# Revit family: IS_Concept_Multiproduct_BIM_GB_E0319;E0320
name_source: partatom
category: Casework
revit_build: Autodesk Revit 2015 (Build: 20140606_1530(x64)
units: mm (PartAtom-declared; Revit-internal decimal feet)

## types (4) — shared parameters
Accessories = www.idealspec.co.uk
AreaUnits = millimeters
Assembly Code = C1030200
AssetType = Fixed
Brand = Ideal Standard
CodePerformance = FSC, EN 14749:2005
ConnectionType = Mechanical
Default Elevation = 2000 mm
Depth = 170 mm
DurationUnit = year
ExpectedLife = 30
Height = 700 mm
IfcExportAs = IfcFurnitureType
IfcExportType = Bathroom cabinets
InstallationInstructions = www.idealspec.co.uk/resources.html
LinearUnits = millimeters
ManufacturerURL = www.idealspec.co.uk
Material = Varies, see product information
MetalMtl = ISI_IdealStandard_Furniture_Metal_Chrome_Render
MirrorMtl = ISI_IdealStandard_Furniture_Mirror_Render
NBSDescription = Bathroom integrated furniture
NBSReference = 45-35-72/320
NominalDepth = 170 mm
NominalHeight = 700 mm
Shape = Rectangular
Space = Internal
SpareParts = www.fastpart-spares.co.uk
Style = Bathroom cabinets
SustainabilityPerformance = FSC
URL = www.idealspec.co.uk
Uniclass2015Code = Pr_40_30_78_03
Uniclass2015Title = Bathroom cabinets
Uniclass2015Version = Products v1.1
Version = 2
VolumeUnits = Litres
WarrantyDescription = Manufacturers warranty
WarrantyDurationParts = 5
WarrantyDurationUnit = year
zero-valued in all types: Cost

## per-type parameters (varying)
| type | 1Door | 2Doors | BIMObjectName | Color | Description | Features | Finish | LaminateMtl | MainColor | Model | ModelNumber | ModelReference | Name | NettWeight | NominalLength | NominalWidth | ProductInformation | Size | Width |
| E0332WG - Concept Space 600 mm Mirror Cabinet - White Gloss | No | Yes | ISI_IdealStandard_BathroomCabinets_Concept_E0332WG | White Gloss | Concept space 600 mm mirror cabinet, white gloss | 600 mm mirror cabinet, white gloss | White Gloss | ISI_IdealStandard_Furniture_Laminate_White_WG_Render | White Gloss | E0320WG | E0332WG | Concept space 600 mm mirror cabinet, white gloss | BathroomCabinets_Concept_E0332WG_IdealStandard | 17.5 Kg | 600 mm | 600 mm | www.idealspec.co.uk/assets/datasheet/E0332WG | 600 x 170 x 700 mm | 600 mm |
| E0331WG - Concept Space 500 mm Mirror Cabinet - White Gloss | Yes | No | ISI_IdealStandard_BathroomCabinets_Concept_E0331WG | White Gloss | Concept space 500 mm mirror cabinet, white gloss | 500 mm mirror cabinet, white gloss | White Gloss | ISI_IdealStandard_Furniture_Laminate_White_WG_Render | White Gloss | E0319WG | E0331WG | Concept space 500 mm mirror cabinet, white gloss | BathroomCabinets_Concept_E0331WG_IdealStandard | 16 Kg | 500 mm  [stored 1.64042 ft] | 500 mm  [stored 1.64042 ft] | www.idealspec.co.uk/assets/datasheet/E0331WG | 500 x 170 x 700 mm | 500 mm  [stored 1.64042 ft] |
| E0332KP - Concept Space 600 mm Mirror Cabinet - Inox | No | Yes | ISI_IdealStandard_BathroomCabinets_Concept_E0332KP | Inox | Concept space 600 mm mirror cabinet, inox | 600 mm mirror cabinet, inox | Inox | ISI_IdealStandard_Furniture_Metal_Aluminium_KP_Render | Inox | E0320KP | E0332KP | Concept space 600 mm mirror cabinet, inox | BathroomCabinets_Concept_E0332KP_IdealStandard | 17.5 Kg | 600 mm | 600 mm | www.idealspec.co.uk/assets/datasheet/E0332KP | 600 x 170 x 700 mm | 600 mm |
| E0331KP - Concept Space 500 mm Mirror Cabinet - Inox | Yes | No | ISI_IdealStandard_BathroomCabinets_Concept_E0331KP | Inox | Concept space 500 mm mirror cabinet, inox | 500 mm mirror cabinet, inox | Inox | ISI_IdealStandard_Furniture_Metal_Aluminium_KP_Render | Inox | E0319KP | E0331KP | Concept space 500 mm mirror cabinet, inox | BathroomCabinets_Concept_E0331KP_IdealStandard | 16 Kg | 500 mm  [stored 1.64042 ft] | 500 mm  [stored 1.64042 ft] | www.idealspec.co.uk/assets/datasheet/E0331KP | 500 x 170 x 700 mm | 500 mm  [stored 1.64042 ft] |

note: [stored X ft] marks values corroborated as IEEE doubles in the binary element streams (Revit-internal decimal feet)

## geometry (parser evidence)
native form markers: Blend x2, Sweep x1
no freeform markers — native parametric forms only
